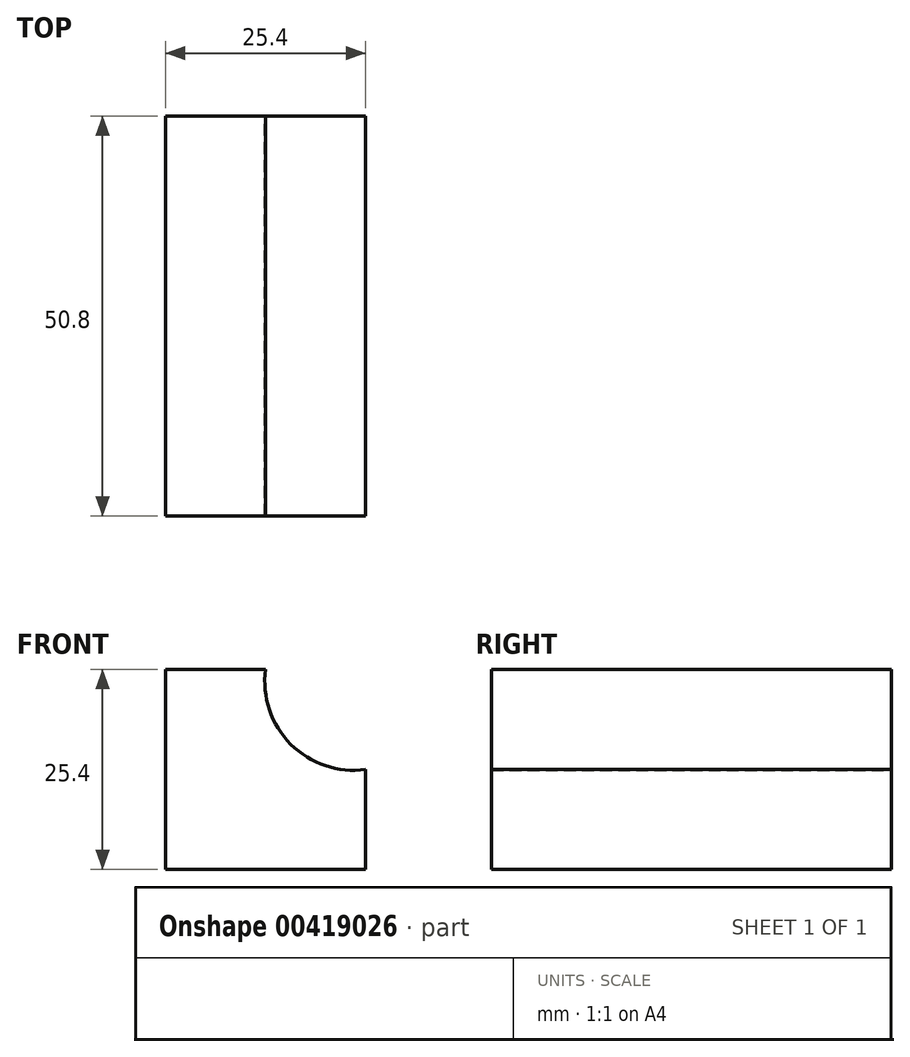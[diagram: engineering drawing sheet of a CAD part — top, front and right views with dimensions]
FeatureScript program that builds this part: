
annotation { "Feature Type Name" : "Feature", "Feature Type Description" : "" }
export const myFeature = defineFeature(function(context is Context, id is Id, definition is map)
    precondition{}
    {
        {
            var Q0;
            Q0=qCreatedBy(makeId("Front.planeOp"),FACE);
            var sketch = newSketch(context, id + "F0", { "sketchPlane" : qUnion([Q0])});
            skLineSegment(sketch, "E0", {"start": v(0, 0) * mm, "end": v(0, 12.7) * mm});
            skLineSegment(sketch, "E1", {"start": v(-12.7, 25.4) * mm, "end": v(-25.4, 25.4) * mm});
            skLineSegment(sketch, "E2", {"start": v(-25.4, 25.4) * mm, "end": v(-25.4, 0) * mm});
            skLineSegment(sketch, "E3", {"start": v(-25.4, 0) * mm, "end": v(0, 0) * mm});
            skArc(sketch, "E4", {"start": v(-12.7, 25.4) * mm, "mid": v(-9.5, 15.9) * mm, "end": v(0, 12.7) * mm});
            skPoint(sketch, "E5.orphan", {"position": v(0, 25.4) * mm});
            skSolve(sketch);
        }
        {
            var Q0;
            Q0 = qSketchRegion(id + "F0", true);
            var Q1;
            Q1=makeQuery(id+"F0.imprint","IMPRINT",FACE,{"disambiguationData":[TD([[makeQuery(id+"F0.imprint","IMPRINT",EDGE,{"derivedFrom":sQuery(id+"F0.wireOp",EDGE,"E0")}),1.0]])]});
            extrude(context, id + "F1", {"entities" : qUnion([Q0, Q1]), "depth" : 50.8 * mm});
        }
    });
